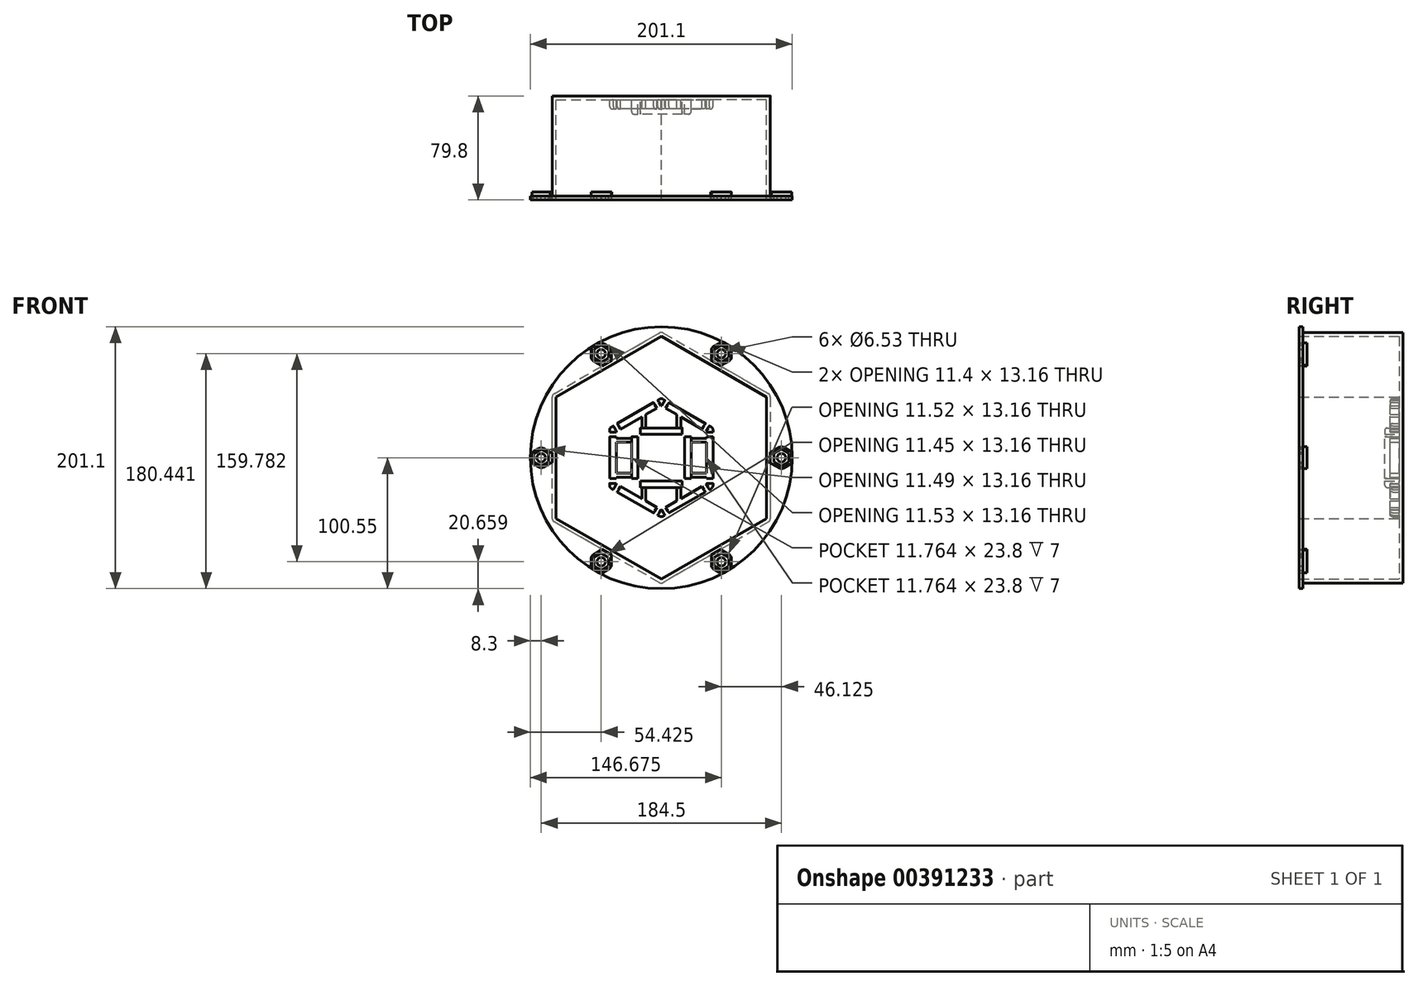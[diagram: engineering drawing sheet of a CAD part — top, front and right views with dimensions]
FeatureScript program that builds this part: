
annotation { "Feature Type Name" : "Feature", "Feature Type Description" : "" }
export const myFeature = defineFeature(function(context is Context, id is Id, definition is map)
    precondition{}
    {
        {
            var Q0;
            Q0=qCreatedBy(makeId("Front.planeOp"),FACE);
            var sketch = newSketch(context, id + "F0", { "sketchPlane" : qUnion([Q0])});
            skCircle(sketch, "E0.cCircle", {"center": v(0, 0) * mm, "radius": 80.75 * mm, "construction": true});
            skLineSegment(sketch, "E0.0", {"start": v(80.75, -46.62) * mm, "end": v(0, -93.24) * mm});
            skLineSegment(sketch, "E0.1", {"start": v(0, -93.24) * mm, "end": v(-80.75, -46.62) * mm});
            skLineSegment(sketch, "E0.2", {"start": v(-80.75, -46.62) * mm, "end": v(-80.75, 46.62) * mm});
            skLineSegment(sketch, "E0.3", {"start": v(-80.75, 46.62) * mm, "end": v(0, 93.24) * mm});
            skLineSegment(sketch, "E0.4", {"start": v(0, 93.24) * mm, "end": v(80.75, 46.62) * mm});
            skLineSegment(sketch, "E0.5", {"start": v(80.75, 46.62) * mm, "end": v(80.75, -46.62) * mm});
            skPoint(sketch, "E0.0.midPoint", {"position": v(40.38, -69.93) * mm});
            skCircle(sketch, "E1.cCircle", {"center": v(0, 0) * mm, "radius": 83.75 * mm, "construction": true});
            skLineSegment(sketch, "E1.0", {"start": v(83.75, 46.62) * mm, "end": v(83.75, -46.62) * mm});
            skLineSegment(sketch, "E1.1", {"start": v(82.25, -49.22) * mm, "end": v(1.5, -95.84) * mm});
            skLineSegment(sketch, "E1.2", {"start": v(-1.5, -95.84) * mm, "end": v(-82.25, -49.22) * mm});
            skLineSegment(sketch, "E1.3", {"start": v(-83.75, -46.62) * mm, "end": v(-83.75, 46.62) * mm});
            skLineSegment(sketch, "E1.4", {"start": v(-82.25, 49.22) * mm, "end": v(-1.5, 95.84) * mm});
            skLineSegment(sketch, "E1.5", {"start": v(1.5, 95.84) * mm, "end": v(82.25, 49.22) * mm});
            skPoint(sketch, "E1.0.midPoint", {"position": v(83.75, 0) * mm});
            skCircle(sketch, "E2", {"center": v(0, 0) * mm, "radius": 100.55 * mm});
            skCircle(sketch, "E3.cCircle", {"center": v(0, 0) * mm, "radius": 39.66 * mm, "construction": true});
            skLineSegment(sketch, "E3.0", {"start": v(38.16, -23.77) * mm, "end": v(1.5, -44.93) * mm});
            skLineSegment(sketch, "E3.1", {"start": v(-1.5, -44.93) * mm, "end": v(-38.16, -23.77) * mm});
            skLineSegment(sketch, "E3.2", {"start": v(-39.66, -21.17) * mm, "end": v(-39.66, 21.17) * mm});
            skLineSegment(sketch, "E3.3", {"start": v(-38.16, 23.77) * mm, "end": v(-1.5, 44.93) * mm});
            skLineSegment(sketch, "E3.4", {"start": v(1.5, 44.93) * mm, "end": v(38.16, 23.77) * mm});
            skLineSegment(sketch, "E3.5", {"start": v(39.66, 21.17) * mm, "end": v(39.66, -21.17) * mm});
            skPoint(sketch, "E3.0.midPoint", {"position": v(19.83, -34.35) * mm});
            skCircle(sketch, "E4.cCircle", {"center": v(0, 0) * mm, "radius": 34.66 * mm, "construction": true});
            skLineSegment(sketch, "E4.0", {"start": v(34.66, -20.01) * mm, "end": v(0, -40.03) * mm});
            skLineSegment(sketch, "E4.1", {"start": v(0, -40.03) * mm, "end": v(-34.66, -20.01) * mm});
            skLineSegment(sketch, "E4.2", {"start": v(-34.66, -20.01) * mm, "end": v(-34.66, 20.01) * mm});
            skLineSegment(sketch, "E4.3", {"start": v(-34.66, 20.01) * mm, "end": v(0, 40.03) * mm});
            skLineSegment(sketch, "E4.4", {"start": v(0, 40.03) * mm, "end": v(34.66, 20.01) * mm});
            skLineSegment(sketch, "E4.5", {"start": v(34.66, 20.01) * mm, "end": v(34.66, -20.01) * mm});
            skPoint(sketch, "E4.0.midPoint", {"position": v(17.33, -30.02) * mm});
            skPoint(sketch, "E5.visualSharp", {"position": v(0, 96.7) * mm});
            skArc(sketch, "E5.filletArc", {"start": v(1.5, 95.84) * mm, "mid": v(0, 96.24) * mm, "end": v(-1.5, 95.84) * mm});
            skPoint(sketch, "E6.visualSharp", {"position": v(83.75, 48.35) * mm});
            skArc(sketch, "E6.filletArc", {"start": v(83.75, 46.62) * mm, "mid": v(83.35, 48.12) * mm, "end": v(82.25, 49.22) * mm});
            skPoint(sketch, "E7.visualSharp", {"position": v(83.75, -48.35) * mm});
            skArc(sketch, "E7.filletArc", {"start": v(82.25, -49.22) * mm, "mid": v(83.35, -48.12) * mm, "end": v(83.75, -46.62) * mm});
            skPoint(sketch, "E8.visualSharp", {"position": v(0, -96.7) * mm});
            skArc(sketch, "E8.filletArc", {"start": v(-1.5, -95.84) * mm, "mid": v(0, -96.24) * mm, "end": v(1.5, -95.84) * mm});
            skPoint(sketch, "E9.visualSharp", {"position": v(-83.75, -48.35) * mm});
            skArc(sketch, "E9.filletArc", {"start": v(-83.75, -46.62) * mm, "mid": v(-83.35, -48.12) * mm, "end": v(-82.25, -49.22) * mm});
            skPoint(sketch, "E10.visualSharp", {"position": v(-83.75, 48.35) * mm});
            skArc(sketch, "E10.filletArc", {"start": v(-82.25, 49.22) * mm, "mid": v(-83.35, 48.12) * mm, "end": v(-83.75, 46.62) * mm});
            skPoint(sketch, "E11.visualSharp", {"position": v(39.66, 22.9) * mm});
            skArc(sketch, "E11.filletArc", {"start": v(39.66, 21.17) * mm, "mid": v(39.26, 22.67) * mm, "end": v(38.16, 23.77) * mm});
            skPoint(sketch, "E12.visualSharp", {"position": v(39.66, -22.9) * mm});
            skArc(sketch, "E12.filletArc", {"start": v(38.16, -23.77) * mm, "mid": v(39.26, -22.67) * mm, "end": v(39.66, -21.17) * mm});
            skPoint(sketch, "E13.visualSharp", {"position": v(0, -45.8) * mm});
            skArc(sketch, "E13.filletArc", {"start": v(-1.5, -44.93) * mm, "mid": v(0, -45.34) * mm, "end": v(1.5, -44.93) * mm});
            skPoint(sketch, "E14.visualSharp", {"position": v(-39.66, -22.9) * mm});
            skArc(sketch, "E14.filletArc", {"start": v(-39.66, -21.17) * mm, "mid": v(-39.26, -22.67) * mm, "end": v(-38.16, -23.77) * mm});
            skPoint(sketch, "E15.visualSharp", {"position": v(-39.66, 22.9) * mm});
            skArc(sketch, "E15.filletArc", {"start": v(-38.16, 23.77) * mm, "mid": v(-39.26, 22.67) * mm, "end": v(-39.66, 21.17) * mm});
            skPoint(sketch, "E16.visualSharp", {"position": v(0, 45.8) * mm});
            skArc(sketch, "E16.filletArc", {"start": v(1.5, 44.93) * mm, "mid": v(0, 45.34) * mm, "end": v(-1.5, 44.93) * mm});
            skPoint(sketch, "E17", {"position": v(-46.13, 79.9) * mm});
            skPoint(sketch, "E18", {"position": v(-92.25, 0) * mm});
            skPoint(sketch, "E19", {"position": v(-46.12, -79.9) * mm});
            skPoint(sketch, "E20", {"position": v(46.13, -79.9) * mm});
            skPoint(sketch, "E21", {"position": v(92.25, 0) * mm});
            skPoint(sketch, "E22", {"position": v(46.13, 79.9) * mm});
            skCircle(sketch, "E23.cCircle", {"center": v(92.25, 0) * mm, "radius": 5.7 * mm, "construction": true});
            skLineSegment(sketch, "E23.0", {"start": v(97.95, -3.3) * mm, "end": v(92.25, -6.58) * mm});
            skLineSegment(sketch, "E23.1", {"start": v(92.25, -6.58) * mm, "end": v(86.55, -3.3) * mm});
            skLineSegment(sketch, "E23.2", {"start": v(86.55, -3.3) * mm, "end": v(86.55, 3.3) * mm});
            skLineSegment(sketch, "E23.3", {"start": v(86.55, 3.3) * mm, "end": v(92.25, 6.58) * mm});
            skLineSegment(sketch, "E23.4", {"start": v(92.25, 6.58) * mm, "end": v(97.95, 3.3) * mm});
            skLineSegment(sketch, "E23.5", {"start": v(97.95, 3.3) * mm, "end": v(97.95, -3.3) * mm});
            skPoint(sketch, "E23.0.midPoint", {"position": v(95.1, -4.94) * mm});
            skCircle(sketch, "E24.cCircle", {"center": v(46.13, 79.9) * mm, "radius": 5.7 * mm, "construction": true});
            skLineSegment(sketch, "E24.0", {"start": v(51.83, 83.18) * mm, "end": v(51.83, 76.6) * mm});
            skLineSegment(sketch, "E24.1", {"start": v(51.83, 76.6) * mm, "end": v(46.13, 73.3) * mm});
            skLineSegment(sketch, "E24.2", {"start": v(46.13, 73.3) * mm, "end": v(40.43, 76.6) * mm});
            skLineSegment(sketch, "E24.3", {"start": v(40.43, 76.6) * mm, "end": v(40.43, 83.18) * mm});
            skLineSegment(sketch, "E24.4", {"start": v(40.43, 83.18) * mm, "end": v(46.12, 86.47) * mm});
            skLineSegment(sketch, "E24.5", {"start": v(46.13, 86.47) * mm, "end": v(51.83, 83.18) * mm});
            skPoint(sketch, "E24.0.midPoint", {"position": v(51.83, 79.9) * mm});
            skCircle(sketch, "E25.cCircle", {"center": v(-46.13, 79.9) * mm, "radius": 5.7 * mm, "construction": true});
            skLineSegment(sketch, "E25.0", {"start": v(-40.5, 76.48) * mm, "end": v(-46.26, 73.31) * mm});
            skLineSegment(sketch, "E25.1", {"start": v(-46.26, 73.31) * mm, "end": v(-51.9, 76.72) * mm});
            skLineSegment(sketch, "E25.2", {"start": v(-51.9, 76.72) * mm, "end": v(-51.76, 83.3) * mm});
            skLineSegment(sketch, "E25.3", {"start": v(-51.76, 83.3) * mm, "end": v(-45.99, 86.47) * mm});
            skLineSegment(sketch, "E25.4", {"start": v(-45.99, 86.47) * mm, "end": v(-40.36, 83.06) * mm});
            skLineSegment(sketch, "E25.5", {"start": v(-40.36, 83.06) * mm, "end": v(-40.5, 76.48) * mm});
            skPoint(sketch, "E25.0.midPoint", {"position": v(-43.38, 74.9) * mm});
            skCircle(sketch, "E26.cCircle", {"center": v(-92.25, 0) * mm, "radius": 5.7 * mm, "construction": true});
            skLineSegment(sketch, "E26.0", {"start": v(-86.5, -3.22) * mm, "end": v(-92.16, -6.58) * mm});
            skLineSegment(sketch, "E26.1", {"start": v(-92.16, -6.58) * mm, "end": v(-97.9, -3.37) * mm});
            skLineSegment(sketch, "E26.2", {"start": v(-97.9, -3.37) * mm, "end": v(-98, 3.22) * mm});
            skLineSegment(sketch, "E26.3", {"start": v(-98, 3.22) * mm, "end": v(-92.34, 6.58) * mm});
            skLineSegment(sketch, "E26.4", {"start": v(-92.34, 6.58) * mm, "end": v(-86.6, 3.37) * mm});
            skLineSegment(sketch, "E26.5", {"start": v(-86.6, 3.37) * mm, "end": v(-86.5, -3.22) * mm});
            skPoint(sketch, "E26.0.midPoint", {"position": v(-89.34, -4.9) * mm});
            skCircle(sketch, "E27.cCircle", {"center": v(46.13, -79.9) * mm, "radius": 5.7 * mm, "construction": true});
            skLineSegment(sketch, "E27.0", {"start": v(51.77, -83.28) * mm, "end": v(46, -86.47) * mm});
            skLineSegment(sketch, "E27.1", {"start": v(46, -86.47) * mm, "end": v(40.37, -83.08) * mm});
            skLineSegment(sketch, "E27.2", {"start": v(40.37, -83.08) * mm, "end": v(40.48, -76.5) * mm});
            skLineSegment(sketch, "E27.3", {"start": v(40.48, -76.5) * mm, "end": v(46.24, -73.31) * mm});
            skLineSegment(sketch, "E27.4", {"start": v(46.24, -73.31) * mm, "end": v(51.88, -76.7) * mm});
            skLineSegment(sketch, "E27.5", {"start": v(51.88, -76.7) * mm, "end": v(51.77, -83.28) * mm});
            skPoint(sketch, "E27.0.midPoint", {"position": v(48.89, -84.88) * mm});
            skCircle(sketch, "E28.cCircle", {"center": v(-46.12, -79.9) * mm, "radius": 5.7 * mm, "construction": true});
            skLineSegment(sketch, "E28.0", {"start": v(-40.4, -83.14) * mm, "end": v(-46.07, -86.47) * mm});
            skLineSegment(sketch, "E28.1", {"start": v(-46.07, -86.47) * mm, "end": v(-51.8, -83.23) * mm});
            skLineSegment(sketch, "E28.2", {"start": v(-51.8, -83.23) * mm, "end": v(-51.85, -76.65) * mm});
            skLineSegment(sketch, "E28.3", {"start": v(-51.85, -76.65) * mm, "end": v(-46.18, -73.3) * mm});
            skLineSegment(sketch, "E28.4", {"start": v(-46.18, -73.3) * mm, "end": v(-40.45, -76.55) * mm});
            skLineSegment(sketch, "E28.5", {"start": v(-40.45, -76.55) * mm, "end": v(-40.4, -83.14) * mm});
            skPoint(sketch, "E28.0.midPoint", {"position": v(-43.24, -84.8) * mm});
            skCircle(sketch, "E29.cCircle", {"center": v(46.13, -79.9) * mm, "radius": 7.7 * mm, "construction": true});
            skLineSegment(sketch, "E29.0", {"start": v(53.87, -77.31) * mm, "end": v(53.78, -82.74) * mm});
            skLineSegment(sketch, "E29.1", {"start": v(52.23, -85.31) * mm, "end": v(47.48, -87.94) * mm});
            skLineSegment(sketch, "E29.2", {"start": v(44.48, -87.89) * mm, "end": v(39.83, -85.1) * mm});
            skLineSegment(sketch, "E29.3", {"start": v(38.38, -82.47) * mm, "end": v(38.5, -75.3) * mm});
            skLineSegment(sketch, "E29.4", {"start": v(38.5, -75.3) * mm, "end": v(46.28, -71) * mm});
            skLineSegment(sketch, "E29.5", {"start": v(46.28, -71) * mm, "end": v(52.42, -74.7) * mm});
            skPoint(sketch, "E29.0.midPoint", {"position": v(53.82, -80.03) * mm});
            skCircle(sketch, "E30.cCircle", {"center": v(-46.12, -79.9) * mm, "radius": 7.7 * mm, "construction": true});
            skLineSegment(sketch, "E30.0", {"start": v(-39.88, -85.15) * mm, "end": v(-44.56, -87.9) * mm});
            skLineSegment(sketch, "E30.1", {"start": v(-47.56, -87.93) * mm, "end": v(-52.28, -85.25) * mm});
            skLineSegment(sketch, "E30.2", {"start": v(-53.8, -82.67) * mm, "end": v(-53.85, -77.24) * mm});
            skLineSegment(sketch, "E30.3", {"start": v(-52.37, -74.63) * mm, "end": v(-46.2, -71) * mm});
            skLineSegment(sketch, "E30.4", {"start": v(-46.2, -71) * mm, "end": v(-38.46, -75.38) * mm});
            skLineSegment(sketch, "E30.5", {"start": v(-38.46, -75.38) * mm, "end": v(-38.4, -82.54) * mm});
            skPoint(sketch, "E30.0.midPoint", {"position": v(-42.22, -86.53) * mm});
            skCircle(sketch, "E31.cCircle", {"center": v(-92.25, 0) * mm, "radius": 7.05 * mm, "construction": true});
            skLineSegment(sketch, "E31.0", {"start": v(-85.15, -3.98) * mm, "end": v(-90.66, -7.25) * mm});
            skLineSegment(sketch, "E31.1", {"start": v(-93.65, -7.3) * mm, "end": v(-97.73, -5) * mm});
            skLineSegment(sketch, "E31.2", {"start": v(-99.27, -2.43) * mm, "end": v(-99.33, 2.24) * mm});
            skLineSegment(sketch, "E31.3", {"start": v(-97.86, 4.86) * mm, "end": v(-93.84, 7.25) * mm});
            skLineSegment(sketch, "E31.4", {"start": v(-90.85, 7.3) * mm, "end": v(-85.26, 4.16) * mm});
            skLineSegment(sketch, "E31.5", {"start": v(-85.26, 4.16) * mm, "end": v(-85.15, -3.98) * mm});
            skPoint(sketch, "E31.0.midPoint", {"position": v(-88.65, -6.06) * mm});
            skCircle(sketch, "E32.cCircle", {"center": v(-46.13, 79.9) * mm, "radius": 7.7 * mm, "construction": true});
            skLineSegment(sketch, "E32.0", {"start": v(-53.83, 77.18) * mm, "end": v(-53.83, 82.6) * mm});
            skLineSegment(sketch, "E32.1", {"start": v(-52.33, 85.2) * mm, "end": v(-47.63, 87.92) * mm});
            skLineSegment(sketch, "E32.2", {"start": v(-44.63, 87.92) * mm, "end": v(-39.93, 85.2) * mm});
            skLineSegment(sketch, "E32.3", {"start": v(-38.43, 82.6) * mm, "end": v(-38.43, 75.45) * mm});
            skLineSegment(sketch, "E32.4", {"start": v(-38.43, 75.45) * mm, "end": v(-46.13, 71) * mm});
            skLineSegment(sketch, "E32.5", {"start": v(-46.13, 71) * mm, "end": v(-52.33, 74.58) * mm});
            skPoint(sketch, "E32.0.midPoint", {"position": v(-53.83, 79.9) * mm});
            skCircle(sketch, "E33.cCircle", {"center": v(46.13, 79.9) * mm, "radius": 7.7 * mm, "construction": true});
            skLineSegment(sketch, "E33.0", {"start": v(52.33, 74.58) * mm, "end": v(46.13, 71) * mm});
            skLineSegment(sketch, "E33.1", {"start": v(46.13, 71) * mm, "end": v(38.43, 75.45) * mm});
            skLineSegment(sketch, "E33.2", {"start": v(38.43, 75.45) * mm, "end": v(38.43, 82.6) * mm});
            skLineSegment(sketch, "E33.3", {"start": v(39.93, 85.2) * mm, "end": v(44.62, 87.92) * mm});
            skLineSegment(sketch, "E33.4", {"start": v(47.62, 87.92) * mm, "end": v(52.33, 85.2) * mm});
            skLineSegment(sketch, "E33.5", {"start": v(53.83, 82.6) * mm, "end": v(53.83, 77.18) * mm});
            skPoint(sketch, "E33.0.midPoint", {"position": v(49.98, 73.22) * mm});
            skCircle(sketch, "E34.cCircle", {"center": v(92.25, 0) * mm, "radius": 7.7 * mm, "construction": true});
            skLineSegment(sketch, "E34.0", {"start": v(99.95, 2.71) * mm, "end": v(99.95, -2.71) * mm});
            skLineSegment(sketch, "E34.1", {"start": v(98.45, -5.31) * mm, "end": v(93.75, -8.03) * mm});
            skLineSegment(sketch, "E34.2", {"start": v(90.75, -8.03) * mm, "end": v(84.55, -4.45) * mm});
            skLineSegment(sketch, "E34.3", {"start": v(84.55, -4.45) * mm, "end": v(84.55, 4.45) * mm});
            skLineSegment(sketch, "E34.4", {"start": v(84.55, 4.45) * mm, "end": v(90.75, 8.03) * mm});
            skLineSegment(sketch, "E34.5", {"start": v(93.75, 8.03) * mm, "end": v(98.45, 5.31) * mm});
            skPoint(sketch, "E34.0.midPoint", {"position": v(99.95, 0) * mm});
            skLineSegment(sketch, "E35", {"start": v(84.55, -4.45) * mm, "end": v(83.75, -4.45) * mm});
            skLineSegment(sketch, "E36", {"start": v(84.55, 4.45) * mm, "end": v(83.75, 4.45) * mm});
            skPoint(sketch, "E37.visualSharp", {"position": v(92.25, 8.9) * mm});
            skArc(sketch, "E37.filletArc", {"start": v(93.75, 8.03) * mm, "mid": v(92.25, 8.43) * mm, "end": v(90.75, 8.03) * mm});
            skPoint(sketch, "E38.visualSharp", {"position": v(99.95, 4.45) * mm});
            skArc(sketch, "E38.filletArc", {"start": v(99.95, 2.71) * mm, "mid": v(99.55, 4.21) * mm, "end": v(98.45, 5.31) * mm});
            skPoint(sketch, "E39.visualSharp", {"position": v(99.95, -4.45) * mm});
            skArc(sketch, "E39.filletArc", {"start": v(98.45, -5.31) * mm, "mid": v(99.55, -4.21) * mm, "end": v(99.95, -2.71) * mm});
            skPoint(sketch, "E40.visualSharp", {"position": v(92.25, -8.9) * mm});
            skArc(sketch, "E40.filletArc", {"start": v(90.75, -8.03) * mm, "mid": v(92.25, -8.43) * mm, "end": v(93.75, -8.03) * mm});
            skPoint(sketch, "E41.visualSharp", {"position": v(38.43, 84.34) * mm});
            skArc(sketch, "E41.filletArc", {"start": v(39.93, 85.2) * mm, "mid": v(38.83, 84.1) * mm, "end": v(38.43, 82.6) * mm});
            skPoint(sketch, "E42.visualSharp", {"position": v(46.12, 88.78) * mm});
            skArc(sketch, "E42.filletArc", {"start": v(47.62, 87.92) * mm, "mid": v(46.12, 88.32) * mm, "end": v(44.62, 87.92) * mm});
            skPoint(sketch, "E43.visualSharp", {"position": v(53.83, 84.34) * mm});
            skArc(sketch, "E43.filletArc", {"start": v(53.83, 82.6) * mm, "mid": v(53.42, 84.1) * mm, "end": v(52.33, 85.2) * mm});
            skPoint(sketch, "E44.visualSharp", {"position": v(53.83, 75.45) * mm});
            skArc(sketch, "E44.filletArc", {"start": v(52.33, 74.58) * mm, "mid": v(53.42, 75.68) * mm, "end": v(53.83, 77.18) * mm});
            skLineSegment(sketch, "E45", {"start": v(38.43, 75.45) * mm, "end": v(38.03, 74.75) * mm});
            skLineSegment(sketch, "E46", {"start": v(46.13, 71) * mm, "end": v(45.73, 70.3) * mm});
            skPoint(sketch, "E47.visualSharp", {"position": v(-46.13, 88.78) * mm});
            skArc(sketch, "E47.filletArc", {"start": v(-44.63, 87.92) * mm, "mid": v(-46.13, 88.32) * mm, "end": v(-47.63, 87.92) * mm});
            skPoint(sketch, "E48.visualSharp", {"position": v(-38.43, 84.34) * mm});
            skArc(sketch, "E48.filletArc", {"start": v(-38.43, 82.6) * mm, "mid": v(-38.83, 84.1) * mm, "end": v(-39.93, 85.2) * mm});
            skPoint(sketch, "E49.visualSharp", {"position": v(-53.83, 84.34) * mm});
            skArc(sketch, "E49.filletArc", {"start": v(-52.33, 85.2) * mm, "mid": v(-53.42, 84.1) * mm, "end": v(-53.83, 82.6) * mm});
            skPoint(sketch, "E50.visualSharp", {"position": v(-53.83, 75.45) * mm});
            skArc(sketch, "E50.filletArc", {"start": v(-53.83, 77.18) * mm, "mid": v(-53.42, 75.68) * mm, "end": v(-52.33, 74.58) * mm});
            skLineSegment(sketch, "E51", {"start": v(-46.13, 71) * mm, "end": v(-45.73, 70.3) * mm});
            skLineSegment(sketch, "E52", {"start": v(-38.43, 75.45) * mm, "end": v(-38.03, 74.75) * mm});
            skPoint(sketch, "E53.visualSharp", {"position": v(-92.36, 8.14) * mm});
            skArc(sketch, "E53.filletArc", {"start": v(-90.85, 7.3) * mm, "mid": v(-92.35, 7.67) * mm, "end": v(-93.84, 7.25) * mm});
            skPoint(sketch, "E54.visualSharp", {"position": v(-99.35, 3.98) * mm});
            skArc(sketch, "E54.filletArc", {"start": v(-97.86, 4.86) * mm, "mid": v(-98.94, 3.75) * mm, "end": v(-99.33, 2.24) * mm});
            skPoint(sketch, "E55.visualSharp", {"position": v(-99.24, -4.16) * mm});
            skArc(sketch, "E55.filletArc", {"start": v(-99.27, -2.43) * mm, "mid": v(-98.84, -3.92) * mm, "end": v(-97.73, -5) * mm});
            skPoint(sketch, "E56.visualSharp", {"position": v(-92.14, -8.14) * mm});
            skArc(sketch, "E56.filletArc", {"start": v(-93.65, -7.3) * mm, "mid": v(-92.15, -7.67) * mm, "end": v(-90.66, -7.25) * mm});
            skLineSegment(sketch, "E57", {"start": v(-85.26, 4.16) * mm, "end": v(-83.75, 4.18) * mm});
            skLineSegment(sketch, "E58", {"start": v(-85.15, -3.98) * mm, "end": v(-83.75, -3.96) * mm});
            skPoint(sketch, "E59.visualSharp", {"position": v(-53.86, -75.5) * mm});
            skArc(sketch, "E59.filletArc", {"start": v(-52.37, -74.63) * mm, "mid": v(-53.46, -75.74) * mm, "end": v(-53.85, -77.24) * mm});
            skPoint(sketch, "E60.visualSharp", {"position": v(-53.79, -84.4) * mm});
            skArc(sketch, "E60.filletArc", {"start": v(-53.8, -82.67) * mm, "mid": v(-53.39, -84.16) * mm, "end": v(-52.28, -85.25) * mm});
            skPoint(sketch, "E61.visualSharp", {"position": v(-46.05, -88.78) * mm});
            skArc(sketch, "E61.filletArc", {"start": v(-47.56, -87.93) * mm, "mid": v(-46.06, -88.32) * mm, "end": v(-44.56, -87.9) * mm});
            skPoint(sketch, "E62.visualSharp", {"position": v(-38.4, -84.28) * mm});
            skArc(sketch, "E62.filletArc", {"start": v(-39.88, -85.15) * mm, "mid": v(-38.8, -84.05) * mm, "end": v(-38.4, -82.54) * mm});
            skLineSegment(sketch, "E63", {"start": v(-46.2, -71) * mm, "end": v(-45.78, -70.27) * mm});
            skLineSegment(sketch, "E64", {"start": v(-38.46, -75.38) * mm, "end": v(-38.08, -74.72) * mm});
            skPoint(sketch, "E65.visualSharp", {"position": v(53.9, -75.58) * mm});
            skArc(sketch, "E65.filletArc", {"start": v(53.87, -77.31) * mm, "mid": v(53.5, -75.8) * mm, "end": v(52.42, -74.7) * mm});
            skPoint(sketch, "E66.visualSharp", {"position": v(53.74, -84.47) * mm});
            skArc(sketch, "E66.filletArc", {"start": v(52.23, -85.31) * mm, "mid": v(53.35, -84.23) * mm, "end": v(53.78, -82.74) * mm});
            skPoint(sketch, "E67.visualSharp", {"position": v(45.97, -88.78) * mm});
            skArc(sketch, "E67.filletArc", {"start": v(44.48, -87.89) * mm, "mid": v(45.97, -88.32) * mm, "end": v(47.48, -87.94) * mm});
            skPoint(sketch, "E68.visualSharp", {"position": v(38.35, -84.2) * mm});
            skArc(sketch, "E68.filletArc", {"start": v(38.38, -82.47) * mm, "mid": v(38.75, -83.97) * mm, "end": v(39.83, -85.1) * mm});
            skLineSegment(sketch, "E69", {"start": v(38.5, -75.3) * mm, "end": v(38.14, -74.68) * mm});
            skLineSegment(sketch, "E70", {"start": v(46.28, -71) * mm, "end": v(45.86, -70.23) * mm});
            skCircle(sketch, "E71.cCircle", {"center": v(0, 0) * mm, "radius": 22.9 * mm, "construction": true});
            skLineSegment(sketch, "E71.0", {"start": v(19.9, -22.9) * mm, "end": v(-19.9, -22.9) * mm});
            skLineSegment(sketch, "E71.1", {"start": v(-22.9, -19.9) * mm, "end": v(-22.9, 19.9) * mm});
            skLineSegment(sketch, "E71.2", {"start": v(-19.9, 22.9) * mm, "end": v(19.9, 22.9) * mm});
            skLineSegment(sketch, "E71.3", {"start": v(22.9, 19.9) * mm, "end": v(22.9, -19.9) * mm});
            skPoint(sketch, "E71.0.midPoint", {"position": v(0, -22.9) * mm});
            skCircle(sketch, "E72.cCircle", {"center": v(0, 0) * mm, "radius": 17.9 * mm, "construction": true});
            skLineSegment(sketch, "E72.0", {"start": v(17.9, -17.9) * mm, "end": v(-17.9, -17.9) * mm});
            skLineSegment(sketch, "E72.1", {"start": v(-17.9, -17.9) * mm, "end": v(-17.9, 17.9) * mm});
            skLineSegment(sketch, "E72.2", {"start": v(-17.9, 17.9) * mm, "end": v(17.9, 17.9) * mm});
            skLineSegment(sketch, "E72.3", {"start": v(17.9, 17.9) * mm, "end": v(17.9, -17.9) * mm});
            skPoint(sketch, "E72.0.midPoint", {"position": v(0, -17.9) * mm});
            skPoint(sketch, "E73.visualSharp", {"position": v(22.9, 22.9) * mm});
            skArc(sketch, "E73.filletArc", {"start": v(22.9, 19.9) * mm, "mid": v(22.02, 22.02) * mm, "end": v(19.9, 22.9) * mm});
            skPoint(sketch, "E74.visualSharp", {"position": v(22.9, -22.9) * mm});
            skArc(sketch, "E74.filletArc", {"start": v(19.9, -22.9) * mm, "mid": v(22.02, -22.02) * mm, "end": v(22.9, -19.9) * mm});
            skPoint(sketch, "E75.visualSharp", {"position": v(-22.9, 22.9) * mm});
            skArc(sketch, "E75.filletArc", {"start": v(-19.9, 22.9) * mm, "mid": v(-22.02, 22.02) * mm, "end": v(-22.9, 19.9) * mm});
            skPoint(sketch, "E76.visualSharp", {"position": v(-22.9, -22.9) * mm});
            skArc(sketch, "E76.filletArc", {"start": v(-22.9, -19.9) * mm, "mid": v(-22.02, -22.02) * mm, "end": v(-19.9, -22.9) * mm});
            skLineSegment(sketch, "E77", {"start": v(-14.9, 22.9) * mm, "end": v(-14.9, 31.42) * mm});
            skLineSegment(sketch, "E78", {"start": v(-11.9, 22.9) * mm, "end": v(-11.9, 33.16) * mm});
            skLineSegment(sketch, "E79", {"start": v(11.9, 22.9) * mm, "end": v(11.9, 33.16) * mm});
            skLineSegment(sketch, "E80", {"start": v(14.9, 22.9) * mm, "end": v(14.9, 31.42) * mm});
            skLineSegment(sketch, "E81", {"start": v(22.9, 14.9) * mm, "end": v(34.66, 14.9) * mm});
            skLineSegment(sketch, "E82", {"start": v(22.9, 11.9) * mm, "end": v(34.66, 11.9) * mm});
            skLineSegment(sketch, "E83", {"start": v(22.9, -14.9) * mm, "end": v(34.66, -14.9) * mm});
            skLineSegment(sketch, "E84", {"start": v(22.9, -11.9) * mm, "end": v(34.66, -11.9) * mm});
            skLineSegment(sketch, "E85", {"start": v(14.9, -22.9) * mm, "end": v(14.9, -31.42) * mm});
            skLineSegment(sketch, "E86", {"start": v(11.9, -22.9) * mm, "end": v(11.9, -33.16) * mm});
            skLineSegment(sketch, "E87", {"start": v(-14.9, -22.9) * mm, "end": v(-14.9, -31.42) * mm});
            skLineSegment(sketch, "E88", {"start": v(-11.9, -22.9) * mm, "end": v(-11.9, -33.16) * mm});
            skLineSegment(sketch, "E89", {"start": v(-22.9, 14.9) * mm, "end": v(-34.66, 14.9) * mm});
            skLineSegment(sketch, "E90", {"start": v(-22.9, 11.9) * mm, "end": v(-34.66, 11.9) * mm});
            skLineSegment(sketch, "E91", {"start": v(-22.9, -11.9) * mm, "end": v(-34.66, -11.9) * mm});
            skLineSegment(sketch, "E92", {"start": v(-22.9, -14.9) * mm, "end": v(-34.66, -14.9) * mm});
            skPoint(sketch, "E93", {"position": v(33.78, 26.3) * mm});
            skPoint(sketch, "E94", {"position": v(36.9, 24.5) * mm});
            skPoint(sketch, "E95", {"position": v(2.77, 44.2) * mm});
            skPoint(sketch, "E96", {"position": v(5.89, 42.4) * mm});
            skLineSegment(sketch, "E97", {"start": v(2.77, 44.2) * mm, "end": v(0.27, 39.87) * mm});
            skLineSegment(sketch, "E98", {"start": v(5.89, 42.4) * mm, "end": v(3.39, 38.07) * mm});
            skLineSegment(sketch, "E99", {"start": v(33.78, 26.3) * mm, "end": v(31.28, 21.97) * mm});
            skLineSegment(sketch, "E100", {"start": v(36.9, 24.5) * mm, "end": v(34.4, 20.17) * mm});
            skPoint(sketch, "E101", {"position": v(-36.9, 24.5) * mm});
            skPoint(sketch, "E102", {"position": v(-33.78, 26.3) * mm});
            skPoint(sketch, "E103", {"position": v(-5.89, 42.4) * mm});
            skPoint(sketch, "E104", {"position": v(-2.77, 44.2) * mm});
            skPoint(sketch, "E105", {"position": v(-39.66, 16.1) * mm});
            skPoint(sketch, "E106", {"position": v(-39.66, -16.1) * mm});
            skPoint(sketch, "E107", {"position": v(-39.66, -19.7) * mm});
            skPoint(sketch, "E108", {"position": v(-36.9, -24.5) * mm});
            skPoint(sketch, "E109", {"position": v(-33.78, -26.3) * mm});
            skPoint(sketch, "E110", {"position": v(-5.89, -42.4) * mm});
            skPoint(sketch, "E111", {"position": v(-2.77, -44.2) * mm});
            skPoint(sketch, "E112", {"position": v(2.77, -44.2) * mm});
            skPoint(sketch, "E113", {"position": v(5.89, -42.4) * mm});
            skPoint(sketch, "E114", {"position": v(33.78, -26.3) * mm});
            skPoint(sketch, "E115", {"position": v(36.9, -24.5) * mm});
            skPoint(sketch, "E116", {"position": v(39.66, -19.7) * mm});
            skPoint(sketch, "E117", {"position": v(39.66, -16.1) * mm});
            skPoint(sketch, "E118", {"position": v(39.66, 16.1) * mm});
            skPoint(sketch, "E119", {"position": v(39.66, 19.7) * mm});
            skPoint(sketch, "E120", {"position": v(-39.66, 19.7) * mm});
            skLineSegment(sketch, "E121", {"start": v(-2.77, 44.2) * mm, "end": v(-0.27, 39.87) * mm});
            skLineSegment(sketch, "E122", {"start": v(-5.89, 42.4) * mm, "end": v(-3.39, 38.07) * mm});
            skLineSegment(sketch, "E123", {"start": v(-39.66, 19.7) * mm, "end": v(-34.66, 19.7) * mm});
            skLineSegment(sketch, "E124", {"start": v(-39.66, 16.1) * mm, "end": v(-34.66, 16.1) * mm});
            skLineSegment(sketch, "E125", {"start": v(-39.66, -16.1) * mm, "end": v(-34.66, -16.1) * mm});
            skLineSegment(sketch, "E126", {"start": v(-39.66, -19.7) * mm, "end": v(-34.66, -19.7) * mm});
            skLineSegment(sketch, "E127", {"start": v(-5.89, -42.4) * mm, "end": v(-3.39, -38.07) * mm});
            skLineSegment(sketch, "E128", {"start": v(-2.77, -44.2) * mm, "end": v(-0.27, -39.87) * mm});
            skLineSegment(sketch, "E129", {"start": v(2.77, -44.2) * mm, "end": v(0.27, -39.87) * mm});
            skLineSegment(sketch, "E130", {"start": v(5.89, -42.4) * mm, "end": v(3.39, -38.07) * mm});
            skLineSegment(sketch, "E131", {"start": v(36.9, -24.5) * mm, "end": v(34.4, -20.17) * mm});
            skLineSegment(sketch, "E132", {"start": v(39.66, -19.7) * mm, "end": v(34.66, -19.7) * mm});
            skLineSegment(sketch, "E133", {"start": v(39.66, -16.1) * mm, "end": v(34.66, -16.1) * mm});
            skLineSegment(sketch, "E134", {"start": v(39.66, 16.1) * mm, "end": v(34.66, 16.1) * mm});
            skLineSegment(sketch, "E135", {"start": v(39.66, 19.7) * mm, "end": v(34.66, 19.7) * mm});
            skLineSegment(sketch, "E136", {"start": v(-33.78, 26.3) * mm, "end": v(-31.28, 21.97) * mm});
            skLineSegment(sketch, "E137", {"start": v(-36.9, 24.5) * mm, "end": v(-34.4, 20.17) * mm});
            skLineSegment(sketch, "E138", {"start": v(-36.9, -24.5) * mm, "end": v(-34.4, -20.17) * mm});
            skLineSegment(sketch, "E139", {"start": v(-33.78, -26.3) * mm, "end": v(-31.28, -21.97) * mm});
            skLineSegment(sketch, "E140", {"start": v(33.78, -26.3) * mm, "end": v(31.28, -21.97) * mm});
            skPoint(sketch, "E141", {"position": v(16.1, 22.9) * mm});
            skLineSegment(sketch, "E142", {"start": v(16.1, 22.9) * mm, "end": v(16.1, 17.9) * mm});
            skPoint(sketch, "E143", {"position": v(22.9, 16.1) * mm});
            skLineSegment(sketch, "E144", {"start": v(22.9, 16.1) * mm, "end": v(17.9, 16.1) * mm});
            skPoint(sketch, "E145", {"position": v(-22.9, 16.1) * mm});
            skPoint(sketch, "E146", {"position": v(-16.1, 22.9) * mm});
            skPoint(sketch, "E147", {"position": v(-22.9, -16.1) * mm});
            skPoint(sketch, "E148", {"position": v(-16.1, -22.9) * mm});
            skPoint(sketch, "E149", {"position": v(16.1, -22.9) * mm});
            skPoint(sketch, "E150", {"position": v(22.9, -16.1) * mm});
            skLineSegment(sketch, "E151", {"start": v(-16.1, 22.9) * mm, "end": v(-16.1, 17.9) * mm});
            skLineSegment(sketch, "E152", {"start": v(-22.9, 16.1) * mm, "end": v(-17.9, 16.1) * mm});
            skLineSegment(sketch, "E153", {"start": v(-22.9, -16.1) * mm, "end": v(-17.9, -16.1) * mm});
            skLineSegment(sketch, "E154", {"start": v(-16.1, -22.9) * mm, "end": v(-16.1, -17.9) * mm});
            skLineSegment(sketch, "E155", {"start": v(16.1, -22.9) * mm, "end": v(16.1, -17.9) * mm});
            skLineSegment(sketch, "E156", {"start": v(22.9, -16.1) * mm, "end": v(17.9, -16.1) * mm});
            skSolve(sketch);
        }
        {
            var Q0;
            Q0=makeQuery(id+"F0.imprint","IMPRINT",FACE,{"disambiguationData":[TD([[makeQuery(id+"F0.imprint","IMPRINT",EDGE,{"derivedFrom":sQuery(id+"F0.wireOp",EDGE,"E0.0")}),-1.0]])]});
            var Q1;
            Q1=makeQuery(id+"F0.imprint","IMPRINT",FACE,{"disambiguationData":[TD([[makeQuery(id+"F0.imprint","IMPRINT",EDGE,{"derivedFrom":sQuery(id+"F0.wireOp",EDGE,"E4.0")}),-1.0]])]});
            var Q2;
            Q2=makeQuery(id+"F0.imprint","IMPRINT",FACE,{"disambiguationData":[TD([[makeQuery(id+"F0.imprint","IMPRINT",EDGE,{"derivedFrom":sQuery(id+"F0.wireOp",EDGE,"E72.0")}),-1.0]])]});
            var Q3;
            {var subQ0=sQuery(id+"F0.wireOp",EDGE,"E75.filletArc");Q3=makeQuery(id+"F0.imprint","IMPRINT",FACE,{"disambiguationData":[TD([[makeQuery(id+"F0.imprint","IMPRINT",EDGE,{"derivedFrom":subQ0}),-1.0]])]});}
            var Q4;
            {var subQ0=sQuery(id+"F0.wireOp",EDGE,"E77");Q4=makeQuery(id+"F0.imprint","IMPRINT",FACE,{"disambiguationData":[TD([[makeQuery(id+"F0.imprint","IMPRINT",EDGE,{"derivedFrom":subQ0}),-1.0]])]});}
            var Q5;
            {var subQ0=sQuery(id+"F0.wireOp",EDGE,"E78");Q5=makeQuery(id+"F0.imprint","IMPRINT",FACE,{"disambiguationData":[TD([[makeQuery(id+"F0.imprint","IMPRINT",EDGE,{"derivedFrom":subQ0}),-1.0]])]});}
            var Q6;
            {var subQ0=sQuery(id+"F0.wireOp",EDGE,"E79");Q6=makeQuery(id+"F0.imprint","IMPRINT",FACE,{"disambiguationData":[TD([[makeQuery(id+"F0.imprint","IMPRINT",EDGE,{"derivedFrom":subQ0}),-1.0]])]});}
            var Q7;
            {var subQ0=sQuery(id+"F0.wireOp",EDGE,"E73.filletArc");Q7=makeQuery(id+"F0.imprint","IMPRINT",FACE,{"disambiguationData":[TD([[makeQuery(id+"F0.imprint","IMPRINT",EDGE,{"derivedFrom":subQ0}),-1.0]])]});}
            var Q8;
            {var subQ0=sQuery(id+"F0.wireOp",EDGE,"E81");Q8=makeQuery(id+"F0.imprint","IMPRINT",FACE,{"disambiguationData":[TD([[makeQuery(id+"F0.imprint","IMPRINT",EDGE,{"derivedFrom":subQ0}),-1.0]])]});}
            var Q9;
            {var subQ0=sQuery(id+"F0.wireOp",EDGE,"E82");Q9=makeQuery(id+"F0.imprint","IMPRINT",FACE,{"disambiguationData":[TD([[makeQuery(id+"F0.imprint","IMPRINT",EDGE,{"derivedFrom":subQ0}),-1.0]])]});}
            var Q10;
            {var subQ0=sQuery(id+"F0.wireOp",EDGE,"E83");Q10=makeQuery(id+"F0.imprint","IMPRINT",FACE,{"disambiguationData":[TD([[makeQuery(id+"F0.imprint","IMPRINT",EDGE,{"derivedFrom":subQ0}),1.0]])]});}
            var Q11;
            {var subQ0=sQuery(id+"F0.wireOp",EDGE,"E74.filletArc");Q11=makeQuery(id+"F0.imprint","IMPRINT",FACE,{"disambiguationData":[TD([[makeQuery(id+"F0.imprint","IMPRINT",EDGE,{"derivedFrom":subQ0}),-1.0]])]});}
            var Q12;
            {var subQ0=sQuery(id+"F0.wireOp",EDGE,"E86");Q12=makeQuery(id+"F0.imprint","IMPRINT",FACE,{"disambiguationData":[TD([[makeQuery(id+"F0.imprint","IMPRINT",EDGE,{"derivedFrom":subQ0}),-1.0]])]});}
            var Q13;
            {var subQ0=sQuery(id+"F0.wireOp",EDGE,"E87");Q13=makeQuery(id+"F0.imprint","IMPRINT",FACE,{"disambiguationData":[TD([[makeQuery(id+"F0.imprint","IMPRINT",EDGE,{"derivedFrom":subQ0}),1.0]])]});}
            var Q14;
            {var subQ0=sQuery(id+"F0.wireOp",EDGE,"E76.filletArc");Q14=makeQuery(id+"F0.imprint","IMPRINT",FACE,{"disambiguationData":[TD([[makeQuery(id+"F0.imprint","IMPRINT",EDGE,{"derivedFrom":subQ0}),-1.0]])]});}
            var Q15;
            {var subQ0=sQuery(id+"F0.wireOp",EDGE,"E91");Q15=makeQuery(id+"F0.imprint","IMPRINT",FACE,{"disambiguationData":[TD([[makeQuery(id+"F0.imprint","IMPRINT",EDGE,{"derivedFrom":subQ0}),1.0]])]});}
            var Q16;
            {var subQ0=sQuery(id+"F0.wireOp",EDGE,"E90");Q16=makeQuery(id+"F0.imprint","IMPRINT",FACE,{"disambiguationData":[TD([[makeQuery(id+"F0.imprint","IMPRINT",EDGE,{"derivedFrom":subQ0}),1.0]])]});}
            var Q17;
            {var subQ0=sQuery(id+"F0.wireOp",EDGE,"E89");Q17=makeQuery(id+"F0.imprint","IMPRINT",FACE,{"disambiguationData":[TD([[makeQuery(id+"F0.imprint","IMPRINT",EDGE,{"derivedFrom":subQ0}),1.0]])]});}
            var Q18;
            {var subQ0=sQuery(id+"F0.wireOp",EDGE,"E97");Q18=makeQuery(id+"F0.imprint","IMPRINT",FACE,{"disambiguationData":[TD([[makeQuery(id+"F0.imprint","IMPRINT",EDGE,{"derivedFrom":subQ0}),1.0]])]});}
            var Q19;
            {var subQ0=sQuery(id+"F0.wireOp",EDGE,"E99");Q19=makeQuery(id+"F0.imprint","IMPRINT",FACE,{"disambiguationData":[TD([[makeQuery(id+"F0.imprint","IMPRINT",EDGE,{"derivedFrom":subQ0}),1.0]])]});}
            var Q20;
            {var subQ0=sQuery(id+"F0.wireOp",EDGE,"E121");Q20=makeQuery(id+"F0.imprint","IMPRINT",FACE,{"disambiguationData":[TD([[makeQuery(id+"F0.imprint","IMPRINT",EDGE,{"derivedFrom":subQ0}),-1.0]])]});}
            var Q21;
            {var subQ0=sQuery(id+"F0.wireOp",EDGE,"E123");Q21=makeQuery(id+"F0.imprint","IMPRINT",FACE,{"disambiguationData":[TD([[makeQuery(id+"F0.imprint","IMPRINT",EDGE,{"derivedFrom":subQ0}),-1.0]])]});}
            var Q22;
            {var subQ0=sQuery(id+"F0.wireOp",EDGE,"E125");Q22=makeQuery(id+"F0.imprint","IMPRINT",FACE,{"disambiguationData":[TD([[makeQuery(id+"F0.imprint","IMPRINT",EDGE,{"derivedFrom":subQ0}),-1.0]])]});}
            var Q23;
            {var subQ0=sQuery(id+"F0.wireOp",EDGE,"E127");Q23=makeQuery(id+"F0.imprint","IMPRINT",FACE,{"disambiguationData":[TD([[makeQuery(id+"F0.imprint","IMPRINT",EDGE,{"derivedFrom":subQ0}),-1.0]])]});}
            var Q24;
            {var subQ0=sQuery(id+"F0.wireOp",EDGE,"E129");Q24=makeQuery(id+"F0.imprint","IMPRINT",FACE,{"disambiguationData":[TD([[makeQuery(id+"F0.imprint","IMPRINT",EDGE,{"derivedFrom":subQ0}),-1.0]])]});}
            var Q25;
            {var subQ0=sQuery(id+"F0.wireOp",EDGE,"E131");Q25=makeQuery(id+"F0.imprint","IMPRINT",FACE,{"disambiguationData":[TD([[makeQuery(id+"F0.imprint","IMPRINT",EDGE,{"derivedFrom":subQ0}),1.0]])]});}
            var Q26;
            {var subQ0=sQuery(id+"F0.wireOp",EDGE,"E132");Q26=makeQuery(id+"F0.imprint","IMPRINT",FACE,{"disambiguationData":[TD([[makeQuery(id+"F0.imprint","IMPRINT",EDGE,{"derivedFrom":subQ0}),-1.0]])]});}
            var Q27;
            {var subQ0=sQuery(id+"F0.wireOp",EDGE,"E134");Q27=makeQuery(id+"F0.imprint","IMPRINT",FACE,{"disambiguationData":[TD([[makeQuery(id+"F0.imprint","IMPRINT",EDGE,{"derivedFrom":subQ0}),-1.0]])]});}
            var Q28;
            {var subQ0=sQuery(id+"F0.wireOp",EDGE,"E136");Q28=makeQuery(id+"F0.imprint","IMPRINT",FACE,{"disambiguationData":[TD([[makeQuery(id+"F0.imprint","IMPRINT",EDGE,{"derivedFrom":subQ0}),-1.0]])]});}
            var Q29;
            {var subQ0=sQuery(id+"F0.wireOp",EDGE,"E138");Q29=makeQuery(id+"F0.imprint","IMPRINT",FACE,{"disambiguationData":[TD([[makeQuery(id+"F0.imprint","IMPRINT",EDGE,{"derivedFrom":subQ0}),-1.0]])]});}
            var Q30;
            {var subQ4=sQuery(id+"F0.wireOp",EDGE,"E73.filletArc");Q30=makeQuery(id+"F0.imprint","IMPRINT",FACE,{"disambiguationData":[TD([[makeQuery(id+"F0.imprint","IMPRINT",EDGE,{"derivedFrom":subQ4}),1.0]])]});}
            var Q31;
            {var subQ4=sQuery(id+"F0.wireOp",EDGE,"E75.filletArc");Q31=makeQuery(id+"F0.imprint","IMPRINT",FACE,{"disambiguationData":[TD([[makeQuery(id+"F0.imprint","IMPRINT",EDGE,{"derivedFrom":subQ4}),1.0]])]});}
            var Q32;
            {var subQ4=sQuery(id+"F0.wireOp",EDGE,"E76.filletArc");Q32=makeQuery(id+"F0.imprint","IMPRINT",FACE,{"disambiguationData":[TD([[makeQuery(id+"F0.imprint","IMPRINT",EDGE,{"derivedFrom":subQ4}),1.0]])]});}
            var Q33;
            {var subQ5=sQuery(id+"F0.wireOp",EDGE,"E74.filletArc");Q33=makeQuery(id+"F0.imprint","IMPRINT",FACE,{"disambiguationData":[TD([[makeQuery(id+"F0.imprint","IMPRINT",EDGE,{"derivedFrom":subQ5}),1.0]])]});}
            var Q34;
            {var subQ0=sQuery(id+"F0.wireOp",EDGE,"E85");Q34=makeQuery(id+"F0.imprint","IMPRINT",FACE,{"disambiguationData":[TD([[makeQuery(id+"F0.imprint","IMPRINT",EDGE,{"derivedFrom":subQ0}),-1.0]])]});}
            extrude(context, id + "F1", {"entities" : qUnion([Q0, Q1, Q2, Q3, Q4, Q5, Q6, Q7, Q8, Q9, Q10, Q11, Q12, Q13, Q14, Q15, Q16, Q17, Q18, Q19, Q20, Q21, Q22, Q23, Q24, Q25, Q26, Q27, Q28, Q29, Q30, Q31, Q32, Q33, Q34]), "depth" : 3 * mm});
        }
        {
            var Q0;
            Q0=makeQuery(id+"F0.imprint","IMPRINT",FACE,{"disambiguationData":[TD([[makeQuery(id+"F0.imprint","IMPRINT",EDGE,{"derivedFrom":sQuery(id+"F0.wireOp",EDGE,"E0.0")}),1.0]])]});
            extrude(context, id + "F2", {"entities" : qUnion([Q0]), "operationType" : NewBodyOperationType.ADD, "depth" : 79.8 * mm});
        }
        {
            var Q0;
            Q0=makeQuery(id+"F0.imprint","IMPRINT",FACE,{"disambiguationData":[TD([[makeQuery(id+"F0.imprint","IMPRINT",EDGE,{"derivedFrom":sQuery(id+"F0.wireOp",EDGE,"E1.0")}),1.0]])]});
            var Q1;
            Q1=makeQuery(id+"F0.imprint","IMPRINT",FACE,{"disambiguationData":[TD([[makeQuery(id+"F0.imprint","IMPRINT",EDGE,{"derivedFrom":sQuery(id+"F0.wireOp",EDGE,"E25.0")}),-1.0]])]});
            var Q2;
            Q2=makeQuery(id+"F0.imprint","IMPRINT",FACE,{"disambiguationData":[TD([[makeQuery(id+"F0.imprint","IMPRINT",EDGE,{"derivedFrom":sQuery(id+"F0.wireOp",EDGE,"E24.0")}),-1.0]])]});
            var Q3;
            Q3=makeQuery(id+"F0.imprint","IMPRINT",FACE,{"disambiguationData":[TD([[makeQuery(id+"F0.imprint","IMPRINT",EDGE,{"derivedFrom":sQuery(id+"F0.wireOp",EDGE,"E23.0")}),-1.0]])]});
            var Q4;
            Q4=makeQuery(id+"F0.imprint","IMPRINT",FACE,{"disambiguationData":[TD([[makeQuery(id+"F0.imprint","IMPRINT",EDGE,{"derivedFrom":sQuery(id+"F0.wireOp",EDGE,"E27.0")}),-1.0]])]});
            var Q5;
            Q5=makeQuery(id+"F0.imprint","IMPRINT",FACE,{"disambiguationData":[TD([[makeQuery(id+"F0.imprint","IMPRINT",EDGE,{"derivedFrom":sQuery(id+"F0.wireOp",EDGE,"E28.0")}),-1.0]])]});
            var Q6;
            Q6=makeQuery(id+"F0.imprint","IMPRINT",FACE,{"disambiguationData":[TD([[makeQuery(id+"F0.imprint","IMPRINT",EDGE,{"derivedFrom":sQuery(id+"F0.wireOp",EDGE,"E26.0")}),-1.0]])]});
            extrude(context, id + "F3", {"entities" : qUnion([Q0, Q1, Q2, Q3, Q4, Q5, Q6]), "operationType" : NewBodyOperationType.ADD, "depth" : 79.8 * mm, "hasSecondDirection" : true, "secondDirectionOppositeDirection" : false, "secondDirectionDepth" : 76.8 * mm});
        }
        {
            var Q0;
            Q0=makeQuery(id+"F0.imprint","IMPRINT",FACE,{"disambiguationData":[TD([[makeQuery(id+"F0.imprint","IMPRINT",EDGE,{"derivedFrom":sQuery(id+"F0.wireOp",EDGE,"E25.0")}),1.0]])]});
            var Q1;
            Q1=makeQuery(id+"F0.imprint","IMPRINT",FACE,{"disambiguationData":[TD([[makeQuery(id+"F0.imprint","IMPRINT",EDGE,{"derivedFrom":sQuery(id+"F0.wireOp",EDGE,"E32.4")}),1.0]])]});
            var Q2;
            Q2=makeQuery(id+"F0.imprint","IMPRINT",FACE,{"disambiguationData":[TD([[makeQuery(id+"F0.imprint","IMPRINT",EDGE,{"derivedFrom":sQuery(id+"F0.wireOp",EDGE,"E24.0")}),1.0]])]});
            var Q3;
            Q3=makeQuery(id+"F0.imprint","IMPRINT",FACE,{"disambiguationData":[TD([[makeQuery(id+"F0.imprint","IMPRINT",EDGE,{"derivedFrom":sQuery(id+"F0.wireOp",EDGE,"E33.1")}),1.0]])]});
            var Q4;
            Q4=makeQuery(id+"F0.imprint","IMPRINT",FACE,{"disambiguationData":[TD([[makeQuery(id+"F0.imprint","IMPRINT",EDGE,{"derivedFrom":sQuery(id+"F0.wireOp",EDGE,"E23.0")}),1.0]])]});
            var Q5;
            Q5=makeQuery(id+"F0.imprint","IMPRINT",FACE,{"disambiguationData":[TD([[makeQuery(id+"F0.imprint","IMPRINT",EDGE,{"derivedFrom":sQuery(id+"F0.wireOp",EDGE,"E34.3")}),1.0]])]});
            var Q6;
            Q6=makeQuery(id+"F0.imprint","IMPRINT",FACE,{"disambiguationData":[TD([[makeQuery(id+"F0.imprint","IMPRINT",EDGE,{"derivedFrom":sQuery(id+"F0.wireOp",EDGE,"E27.0")}),1.0]])]});
            var Q7;
            Q7=makeQuery(id+"F0.imprint","IMPRINT",FACE,{"disambiguationData":[TD([[makeQuery(id+"F0.imprint","IMPRINT",EDGE,{"derivedFrom":sQuery(id+"F0.wireOp",EDGE,"E29.4")}),1.0]])]});
            var Q8;
            Q8=makeQuery(id+"F0.imprint","IMPRINT",FACE,{"disambiguationData":[TD([[makeQuery(id+"F0.imprint","IMPRINT",EDGE,{"derivedFrom":sQuery(id+"F0.wireOp",EDGE,"E28.0")}),1.0]])]});
            var Q9;
            Q9=makeQuery(id+"F0.imprint","IMPRINT",FACE,{"disambiguationData":[TD([[makeQuery(id+"F0.imprint","IMPRINT",EDGE,{"derivedFrom":sQuery(id+"F0.wireOp",EDGE,"E30.4")}),1.0]])]});
            var Q10;
            Q10=makeQuery(id+"F0.imprint","IMPRINT",FACE,{"disambiguationData":[TD([[makeQuery(id+"F0.imprint","IMPRINT",EDGE,{"derivedFrom":sQuery(id+"F0.wireOp",EDGE,"E26.0")}),1.0]])]});
            var Q11;
            Q11=makeQuery(id+"F0.imprint","IMPRINT",FACE,{"disambiguationData":[TD([[makeQuery(id+"F0.imprint","IMPRINT",EDGE,{"derivedFrom":sQuery(id+"F0.wireOp",EDGE,"E31.5")}),1.0]])]});
            extrude(context, id + "F4", {"entities" : qUnion([Q0, Q1, Q2, Q3, Q4, Q5, Q6, Q7, Q8, Q9, Q10, Q11]), "depth" : 79.8 * mm, "hasSecondDirection" : true, "secondDirectionOppositeDirection" : false, "secondDirectionDepth" : 73.8 * mm});
        }
        {
            var Q0;
            Q0=sQuery(id+"F0.wireOp",VERTEX,"E17");
            var Q1;
            Q1=sQuery(id+"F0.wireOp",VERTEX,"E22");
            var Q2;
            Q2=sQuery(id+"F0.wireOp",VERTEX,"E21");
            var Q3;
            Q3=sQuery(id+"F0.wireOp",VERTEX,"E20");
            var Q4;
            Q4=sQuery(id+"F0.wireOp",VERTEX,"E19");
            var Q5;
            Q5=sQuery(id+"F0.wireOp",VERTEX,"E18");
            var Q6;
            Q6=makeQuery(id+"F3.opExtrude","SWEPT_BODY",BODY,{"disambiguationData":[OSD([sQuery(id+"F0.wireOp",EDGE,"E23.0"),sQuery(id+"F0.wireOp",EDGE,"E23.1"),sQuery(id+"F0.wireOp",EDGE,"E23.2"),sQuery(id+"F0.wireOp",EDGE,"E23.3"),sQuery(id+"F0.wireOp",EDGE,"E23.4"),sQuery(id+"F0.wireOp",EDGE,"E23.5")])]});
            var Q7;
            Q7=makeQuery(id+"F3.opExtrude","SWEPT_BODY",BODY,{"disambiguationData":[OSD([sQuery(id+"F0.wireOp",EDGE,"E24.0"),sQuery(id+"F0.wireOp",EDGE,"E24.1"),sQuery(id+"F0.wireOp",EDGE,"E24.2"),sQuery(id+"F0.wireOp",EDGE,"E24.3"),sQuery(id+"F0.wireOp",EDGE,"E24.4"),sQuery(id+"F0.wireOp",EDGE,"E24.5")])]});
            var Q8;
            Q8=makeQuery(id+"F3.opExtrude","SWEPT_BODY",BODY,{"disambiguationData":[OSD([sQuery(id+"F0.wireOp",EDGE,"E25.0"),sQuery(id+"F0.wireOp",EDGE,"E25.1"),sQuery(id+"F0.wireOp",EDGE,"E25.2"),sQuery(id+"F0.wireOp",EDGE,"E25.3"),sQuery(id+"F0.wireOp",EDGE,"E25.4"),sQuery(id+"F0.wireOp",EDGE,"E25.5")])]});
            var Q9;
            Q9=makeQuery(id+"F3.opExtrude","SWEPT_BODY",BODY,{"disambiguationData":[OSD([sQuery(id+"F0.wireOp",EDGE,"E26.0"),sQuery(id+"F0.wireOp",EDGE,"E26.1"),sQuery(id+"F0.wireOp",EDGE,"E26.2"),sQuery(id+"F0.wireOp",EDGE,"E26.3"),sQuery(id+"F0.wireOp",EDGE,"E26.4"),sQuery(id+"F0.wireOp",EDGE,"E26.5")])]});
            var Q10;
            Q10=makeQuery(id+"F3.opExtrude","SWEPT_BODY",BODY,{"disambiguationData":[OSD([sQuery(id+"F0.wireOp",EDGE,"E27.0"),sQuery(id+"F0.wireOp",EDGE,"E27.1"),sQuery(id+"F0.wireOp",EDGE,"E27.2"),sQuery(id+"F0.wireOp",EDGE,"E27.3"),sQuery(id+"F0.wireOp",EDGE,"E27.4"),sQuery(id+"F0.wireOp",EDGE,"E27.5")])]});
            var Q11;
            Q11=makeQuery(id+"F3.opExtrude","SWEPT_BODY",BODY,{"disambiguationData":[OSD([sQuery(id+"F0.wireOp",EDGE,"E28.0"),sQuery(id+"F0.wireOp",EDGE,"E28.1"),sQuery(id+"F0.wireOp",EDGE,"E28.2"),sQuery(id+"F0.wireOp",EDGE,"E28.3"),sQuery(id+"F0.wireOp",EDGE,"E28.4"),sQuery(id+"F0.wireOp",EDGE,"E28.5")])]});
            hole(context, id + "F5", {"style" : HoleStyle.SIMPLE, "endStyle" : HoleEndStyle.THROUGH, "oppositeDirection" : true, "standardTappedOrClearance" : lookupTablePath({ "standard" : "ANSI", "fit" : "Close", "size" : "1/4", "type" : "Clearance" }), "standardBlindInLast" : lookupTablePath({ "fit" : "Close", "standard" : "ANSI", "size" : "1/4", "type" : "Clearance" }), "holeDiameter" : 6.53 * mm, "tappedDepth" : 12 * mm, "tapClearance" : 3, "locations" : qUnion([Q0, Q1, Q2, Q3, Q4, Q5]), "scope" : qUnion([Q6, Q7, Q8, Q9, Q10, Q11])});
        }
        {
            var Q0;
            Q0=makeQuery(id+"F0.imprint","IMPRINT",FACE,{"disambiguationData":[TD([[makeQuery(id+"F0.imprint","IMPRINT",EDGE,{"derivedFrom":sQuery(id+"F0.wireOp",EDGE,"E71.0")}),-1.0]])]});
            var Q1;
            {var subQ3=sQuery(id+"F0.wireOp",EDGE,"E142");Q1=makeQuery(id+"F0.imprint","IMPRINT",FACE,{"disambiguationData":[TD([[makeQuery(id+"F0.imprint","IMPRINT",EDGE,{"derivedFrom":subQ3}),-1.0]])]});}
            var Q2;
            {var subQ5=sQuery(id+"F0.wireOp",EDGE,"E152");Q2=makeQuery(id+"F0.imprint","IMPRINT",FACE,{"disambiguationData":[TD([[makeQuery(id+"F0.imprint","IMPRINT",EDGE,{"derivedFrom":subQ5}),-1.0]])]});}
            var Q3;
            {var subQ6=sQuery(id+"F0.wireOp",EDGE,"E144");Q3=makeQuery(id+"F0.imprint","IMPRINT",FACE,{"disambiguationData":[TD([[makeQuery(id+"F0.imprint","IMPRINT",EDGE,{"derivedFrom":subQ6}),1.0]])]});}
            extrude(context, id + "F6", {"entities" : qUnion([Q0, Q1, Q2, Q3]), "depth" : 14 * mm});
        }
        {
            var Q0;
            Q0=makeQuery(id+"F6.opExtrude","CAP_EDGE",EDGE,{"disambiguationData":[OSD([sQuery(id+"F0.wireOp",EDGE,"E71.3")])],"isStart":false});
            var Q1;
            Q1=makeQuery(id+"F6.opExtrude","CAP_EDGE",EDGE,{"disambiguationData":[OSD([sQuery(id+"F0.wireOp",EDGE,"E71.0")])],"isStart":false});
            var Q2;
            Q2=makeQuery(id+"F6.opExtrude","CAP_EDGE",EDGE,{"disambiguationData":[OSD([sQuery(id+"F0.wireOp",EDGE,"E71.1")])],"isStart":false});
            var Q3;
            Q3=makeQuery(id+"F6.opExtrude","CAP_EDGE",EDGE,{"disambiguationData":[OSD([sQuery(id+"F0.wireOp",EDGE,"E71.2")])],"isStart":false});
            fillet(context, id + "F7", {"entities" : qUnion([Q0, Q1, Q2, Q3]), "radius" : 2 * mm, "tangentPropagation" : true, "allowEdgeOverflow" : false});
        }
        {
            var Q0;
            {var subQ0=sQuery(id+"F0.wireOp",EDGE,"E91");Q0=makeQuery(id+"F0.imprint","IMPRINT",FACE,{"disambiguationData":[TD([[makeQuery(id+"F0.imprint","IMPRINT",EDGE,{"derivedFrom":subQ0}),1.0]])]});}
            var Q1;
            {var subQ0=sQuery(id+"F0.wireOp",EDGE,"E89");Q1=makeQuery(id+"F0.imprint","IMPRINT",FACE,{"disambiguationData":[TD([[makeQuery(id+"F0.imprint","IMPRINT",EDGE,{"derivedFrom":subQ0}),1.0]])]});}
            var Q2;
            {var subQ0=sQuery(id+"F0.wireOp",EDGE,"E77");Q2=makeQuery(id+"F0.imprint","IMPRINT",FACE,{"disambiguationData":[TD([[makeQuery(id+"F0.imprint","IMPRINT",EDGE,{"derivedFrom":subQ0}),-1.0]])]});}
            var Q3;
            {var subQ0=sQuery(id+"F0.wireOp",EDGE,"E79");Q3=makeQuery(id+"F0.imprint","IMPRINT",FACE,{"disambiguationData":[TD([[makeQuery(id+"F0.imprint","IMPRINT",EDGE,{"derivedFrom":subQ0}),-1.0]])]});}
            var Q4;
            {var subQ0=sQuery(id+"F0.wireOp",EDGE,"E81");Q4=makeQuery(id+"F0.imprint","IMPRINT",FACE,{"disambiguationData":[TD([[makeQuery(id+"F0.imprint","IMPRINT",EDGE,{"derivedFrom":subQ0}),-1.0]])]});}
            var Q5;
            {var subQ0=sQuery(id+"F0.wireOp",EDGE,"E83");Q5=makeQuery(id+"F0.imprint","IMPRINT",FACE,{"disambiguationData":[TD([[makeQuery(id+"F0.imprint","IMPRINT",EDGE,{"derivedFrom":subQ0}),1.0]])]});}
            var Q6;
            {var subQ0=sQuery(id+"F0.wireOp",EDGE,"E85");Q6=makeQuery(id+"F0.imprint","IMPRINT",FACE,{"disambiguationData":[TD([[makeQuery(id+"F0.imprint","IMPRINT",EDGE,{"derivedFrom":subQ0}),-1.0]])]});}
            var Q7;
            {var subQ0=sQuery(id+"F0.wireOp",EDGE,"E87");Q7=makeQuery(id+"F0.imprint","IMPRINT",FACE,{"disambiguationData":[TD([[makeQuery(id+"F0.imprint","IMPRINT",EDGE,{"derivedFrom":subQ0}),1.0]])]});}
            var Q8;
            {var subQ3=sQuery(id+"F0.wireOp",EDGE,"E98");Q8=makeQuery(id+"F0.imprint","IMPRINT",FACE,{"disambiguationData":[TD([[makeQuery(id+"F0.imprint","IMPRINT",EDGE,{"derivedFrom":subQ3}),1.0]])]});}
            var Q9;
            {var subQ4=sQuery(id+"F0.wireOp",EDGE,"E16.filletArc");Q9=makeQuery(id+"F0.imprint","IMPRINT",FACE,{"disambiguationData":[TD([[makeQuery(id+"F0.imprint","IMPRINT",EDGE,{"derivedFrom":subQ4}),1.0]])]});}
            var Q10;
            {var subQ4=sQuery(id+"F0.wireOp",EDGE,"E122");Q10=makeQuery(id+"F0.imprint","IMPRINT",FACE,{"disambiguationData":[TD([[makeQuery(id+"F0.imprint","IMPRINT",EDGE,{"derivedFrom":subQ4}),-1.0]])]});}
            var Q11;
            {var subQ4=sQuery(id+"F0.wireOp",EDGE,"E15.filletArc");Q11=makeQuery(id+"F0.imprint","IMPRINT",FACE,{"disambiguationData":[TD([[makeQuery(id+"F0.imprint","IMPRINT",EDGE,{"derivedFrom":subQ4}),1.0]])]});}
            var Q12;
            {var subQ5=sQuery(id+"F0.wireOp",EDGE,"E124");Q12=makeQuery(id+"F0.imprint","IMPRINT",FACE,{"disambiguationData":[TD([[makeQuery(id+"F0.imprint","IMPRINT",EDGE,{"derivedFrom":subQ5}),-1.0]])]});}
            var Q13;
            {var subQ4=sQuery(id+"F0.wireOp",EDGE,"E14.filletArc");Q13=makeQuery(id+"F0.imprint","IMPRINT",FACE,{"disambiguationData":[TD([[makeQuery(id+"F0.imprint","IMPRINT",EDGE,{"derivedFrom":subQ4}),1.0]])]});}
            var Q14;
            {var subQ3=sQuery(id+"F0.wireOp",EDGE,"E127");Q14=makeQuery(id+"F0.imprint","IMPRINT",FACE,{"disambiguationData":[TD([[makeQuery(id+"F0.imprint","IMPRINT",EDGE,{"derivedFrom":subQ3}),1.0]])]});}
            var Q15;
            {var subQ4=sQuery(id+"F0.wireOp",EDGE,"E13.filletArc");Q15=makeQuery(id+"F0.imprint","IMPRINT",FACE,{"disambiguationData":[TD([[makeQuery(id+"F0.imprint","IMPRINT",EDGE,{"derivedFrom":subQ4}),1.0]])]});}
            var Q16;
            {var subQ2=sQuery(id+"F0.wireOp",EDGE,"E130");Q16=makeQuery(id+"F0.imprint","IMPRINT",FACE,{"disambiguationData":[TD([[makeQuery(id+"F0.imprint","IMPRINT",EDGE,{"derivedFrom":subQ2}),-1.0]])]});}
            var Q17;
            {var subQ0=sQuery(id+"F0.wireOp",EDGE,"E12.filletArc");Q17=makeQuery(id+"F0.imprint","IMPRINT",FACE,{"disambiguationData":[TD([[makeQuery(id+"F0.imprint","IMPRINT",EDGE,{"derivedFrom":subQ0}),1.0]])]});}
            var Q18;
            {var subQ3=sQuery(id+"F0.wireOp",EDGE,"E133");Q18=makeQuery(id+"F0.imprint","IMPRINT",FACE,{"disambiguationData":[TD([[makeQuery(id+"F0.imprint","IMPRINT",EDGE,{"derivedFrom":subQ3}),-1.0]])]});}
            var Q19;
            {var subQ5=sQuery(id+"F0.wireOp",EDGE,"E11.filletArc");Q19=makeQuery(id+"F0.imprint","IMPRINT",FACE,{"disambiguationData":[TD([[makeQuery(id+"F0.imprint","IMPRINT",EDGE,{"derivedFrom":subQ5}),1.0]])]});}
            extrude(context, id + "F8", {"entities" : qUnion([Q0, Q1, Q2, Q3, Q4, Q5, Q6, Q7, Q8, Q9, Q10, Q11, Q12, Q13, Q14, Q15, Q16, Q17, Q18, Q19]), "operationType" : NewBodyOperationType.ADD, "depth" : 10 * mm});
        }
        {
            var Q0;
            {var subQ0=sQuery(id+"F0.wireOp",EDGE,"E3.3");Q0=makeQuery(id+"F8.opExtrude","CAP_EDGE",EDGE,{"disambiguationData":[OSD([subQ0]),TDD([makeQuery(id+"F0.imprint","IMPRINT",EDGE,{"disambiguationData":[TD([[makeQuery(id+"F0.imprint","INTERSECT",VERTEX,{"derivedFrom":[subQ0,sQuery(id+"F0.wireOp",EDGE,"E122")]}),1.0]])],"derivedFrom":subQ0})])],"isStart":false});}
            var Q1;
            Q1=makeQuery(id+"F8.opExtrude","CAP_EDGE",EDGE,{"disambiguationData":[OSD([sQuery(id+"F0.wireOp",EDGE,"E15.filletArc")])],"isStart":false});
            var Q2;
            Q2=makeQuery(id+"F8.opExtrude","CAP_EDGE",EDGE,{"disambiguationData":[OSD([sQuery(id+"F0.wireOp",EDGE,"E16.filletArc")])],"isStart":false});
            var Q3;
            Q3=makeQuery(id+"F8.opExtrude","CAP_EDGE",EDGE,{"disambiguationData":[OSD([sQuery(id+"F0.wireOp",EDGE,"E11.filletArc")])],"isStart":false});
            var Q4;
            {var subQ0=sQuery(id+"F0.wireOp",EDGE,"E3.4");Q4=makeQuery(id+"F8.opExtrude","CAP_EDGE",EDGE,{"disambiguationData":[OSD([subQ0]),TDD([makeQuery(id+"F0.imprint","IMPRINT",EDGE,{"disambiguationData":[TD([[makeQuery(id+"F0.imprint","INTERSECT",VERTEX,{"derivedFrom":[subQ0,sQuery(id+"F0.wireOp",EDGE,"E98")]}),-1.0]])],"derivedFrom":subQ0})])],"isStart":false});}
            var Q5;
            {var subQ0=sQuery(id+"F0.wireOp",EDGE,"E3.5");Q5=makeQuery(id+"F8.opExtrude","CAP_EDGE",EDGE,{"disambiguationData":[OSD([subQ0]),TDD([makeQuery(id+"F0.imprint","IMPRINT",EDGE,{"disambiguationData":[TD([[makeQuery(id+"F0.imprint","INTERSECT",VERTEX,{"derivedFrom":[subQ0,sQuery(id+"F0.wireOp",EDGE,"E133")]}),1.0]])],"derivedFrom":subQ0})])],"isStart":false});}
            var Q6;
            {var subQ0=sQuery(id+"F0.wireOp",EDGE,"E3.2");Q6=makeQuery(id+"F8.opExtrude","CAP_EDGE",EDGE,{"disambiguationData":[OSD([subQ0]),TDD([makeQuery(id+"F0.imprint","IMPRINT",EDGE,{"disambiguationData":[TD([[makeQuery(id+"F0.imprint","INTERSECT",VERTEX,{"derivedFrom":[subQ0,sQuery(id+"F0.wireOp",EDGE,"E124")]}),1.0]])],"derivedFrom":subQ0})])],"isStart":false});}
            var Q7;
            Q7=makeQuery(id+"F8.opExtrude","CAP_EDGE",EDGE,{"disambiguationData":[OSD([sQuery(id+"F0.wireOp",EDGE,"E14.filletArc")])],"isStart":false});
            var Q8;
            {var subQ0=sQuery(id+"F0.wireOp",EDGE,"E3.1");Q8=makeQuery(id+"F8.opExtrude","CAP_EDGE",EDGE,{"disambiguationData":[OSD([subQ0]),TDD([makeQuery(id+"F0.imprint","IMPRINT",EDGE,{"disambiguationData":[TD([[makeQuery(id+"F0.imprint","INTERSECT",VERTEX,{"derivedFrom":[subQ0,sQuery(id+"F0.wireOp",EDGE,"E127")]}),-1.0]])],"derivedFrom":subQ0})])],"isStart":false});}
            var Q9;
            Q9=makeQuery(id+"F8.opExtrude","CAP_EDGE",EDGE,{"disambiguationData":[OSD([sQuery(id+"F0.wireOp",EDGE,"E12.filletArc")])],"isStart":false});
            var Q10;
            {var subQ0=sQuery(id+"F0.wireOp",EDGE,"E3.0");Q10=makeQuery(id+"F8.opExtrude","CAP_EDGE",EDGE,{"disambiguationData":[OSD([subQ0]),TDD([makeQuery(id+"F0.imprint","IMPRINT",EDGE,{"disambiguationData":[TD([[makeQuery(id+"F0.imprint","INTERSECT",VERTEX,{"derivedFrom":[subQ0,sQuery(id+"F0.wireOp",EDGE,"E130")]}),1.0]])],"derivedFrom":subQ0})])],"isStart":false});}
            var Q11;
            Q11=makeQuery(id+"F8.opExtrude","CAP_EDGE",EDGE,{"disambiguationData":[OSD([sQuery(id+"F0.wireOp",EDGE,"E13.filletArc")])],"isStart":false});
            fillet(context, id + "F9", {"entities" : qUnion([Q0, Q1, Q2, Q3, Q4, Q5, Q6, Q7, Q8, Q9, Q10, Q11]), "radius" : 2 * mm, "tangentPropagation" : true, "allowEdgeOverflow" : false});
        }
    });
